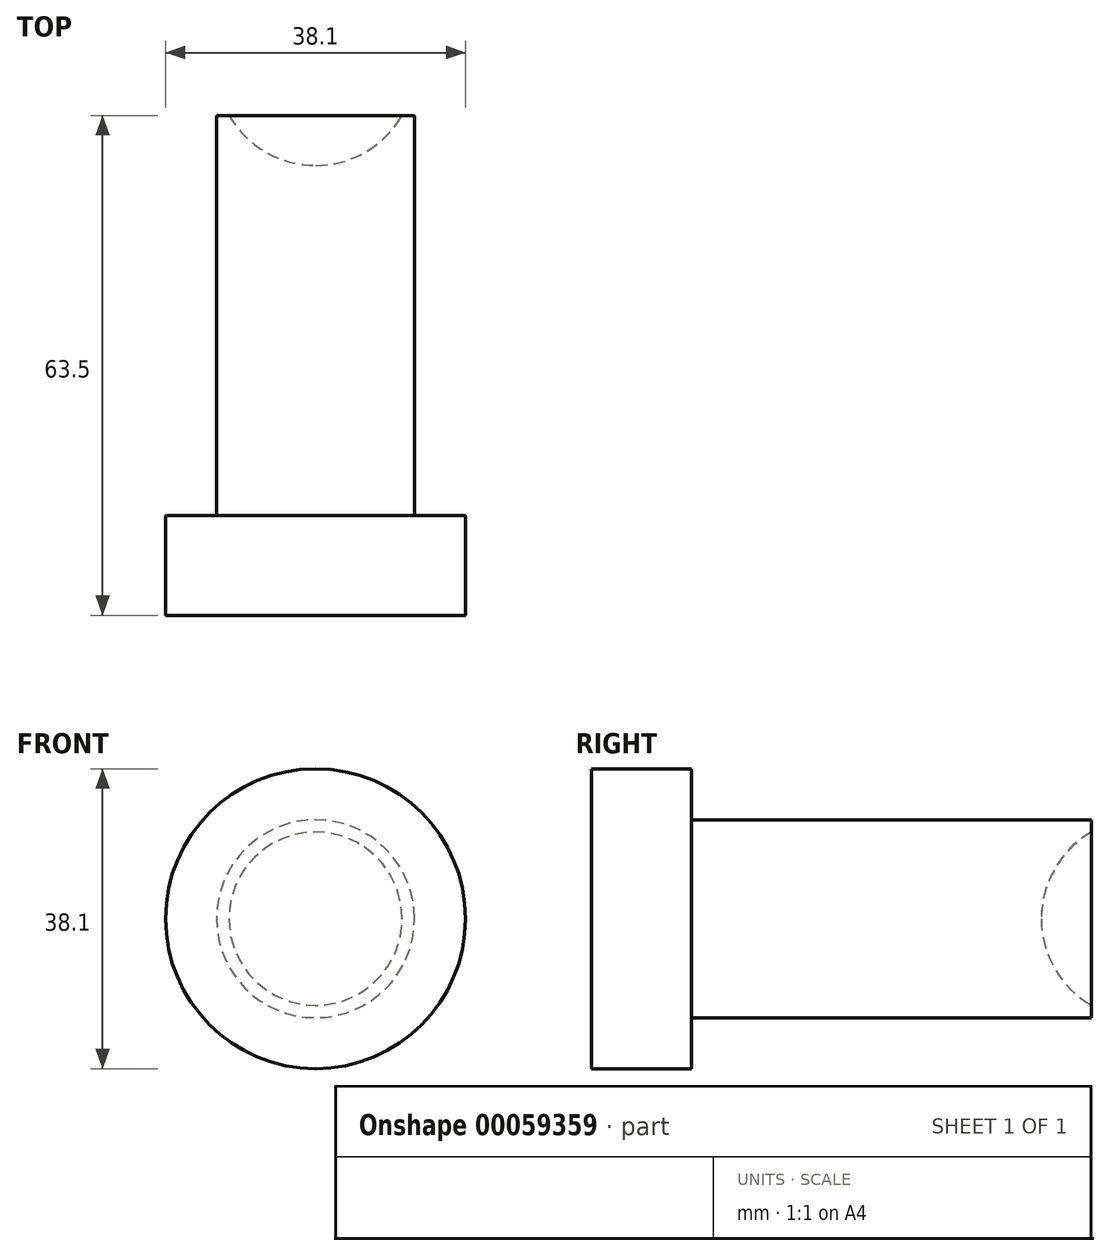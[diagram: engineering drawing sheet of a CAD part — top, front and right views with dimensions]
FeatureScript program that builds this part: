
annotation { "Feature Type Name" : "Feature", "Feature Type Description" : "" }
export const myFeature = defineFeature(function(context is Context, id is Id, definition is map)
    precondition{}
    {
        {
            var Q0;
            Q0=qCreatedBy(makeId("Front.planeOp"),FACE);
            var sketch = newSketch(context, id + "F0", { "sketchPlane" : qUnion([Q0])});
            skCircle(sketch, "E0", {"center": v(0, 0) * mm, "radius": 19.05 * mm});
            skSolve(sketch);
        }
        {
            var Q0;
            Q0=makeQuery(id+"F0.imprint","IMPRINT",FACE,{"disambiguationData":[TD([[makeQuery(id+"F0.imprint","IMPRINT",EDGE,{"derivedFrom":sQuery(id+"F0.wireOp",EDGE,"E0")}),1.0]])]});
            extrude(context, id + "F1", {"entities" : qUnion([Q0]), "depth" : 12.7 * mm});
        }
        {
            var Q0;
            Q0=makeQuery(id+"F1.opExtrude","CAP_FACE",FACE,{"disambiguationData":[OSD([sQuery(id+"F0.wireOp",EDGE,"E0")])],"isStart":true});
            var sketch = newSketch(context, id + "F2", { "sketchPlane" : qUnion([Q0])});
            skCircle(sketch, "E1", {"center": v(0, 0) * mm, "radius": 12.57 * mm});
            skSolve(sketch);
        }
        {
            var Q0;
            Q0=makeQuery(id+"F2.imprint","IMPRINT",FACE,{"disambiguationData":[TD([[makeQuery(id+"F2.imprint","IMPRINT",EDGE,{"derivedFrom":sQuery(id+"F2.wireOp",EDGE,"E1")}),1.0]])]});
            extrude(context, id + "F3", {"entities" : qUnion([Q0]), "operationType" : NewBodyOperationType.ADD, "depth" : 50.8 * mm});
        }
        {
            var Q0;
            Q0=qCreatedBy(makeId("Right.planeOp"),FACE);
            var sketch = newSketch(context, id + "F4", { "sketchPlane" : qUnion([Q0])});
            skArc(sketch, "E2", {"start": v(57.15, 12.7) * mm, "mid": v(48.17, 8.98) * mm, "end": v(44.45, 0) * mm});
            skLineSegment(sketch, "E3", {"start": v(57.15, 12.7) * mm, "end": v(57.15, 0) * mm});
            skLineSegment(sketch, "E4", {"start": v(57.15, 0) * mm, "end": v(44.45, 0) * mm});
            skSolve(sketch);
        }
        {
            var Q0;
            Q0=makeQuery(id+"F4.imprint","IMPRINT",FACE,{"disambiguationData":[TD([[makeQuery(id+"F4.imprint","IMPRINT",EDGE,{"derivedFrom":sQuery(id+"F4.wireOp",EDGE,"E2")}),1.0]])]});
            var Q1;
            Q1=sQuery(id+"F4.wireOp",EDGE,"E4");
            revolve(context, id + "F5", {"operationType" : NewBodyOperationType.REMOVE, "entities" : qUnion([Q0]), "axis" : qUnion([Q1]), "revolveType" : RevolveType.FULL, "oppositeDirection" : true});
        }
    });
